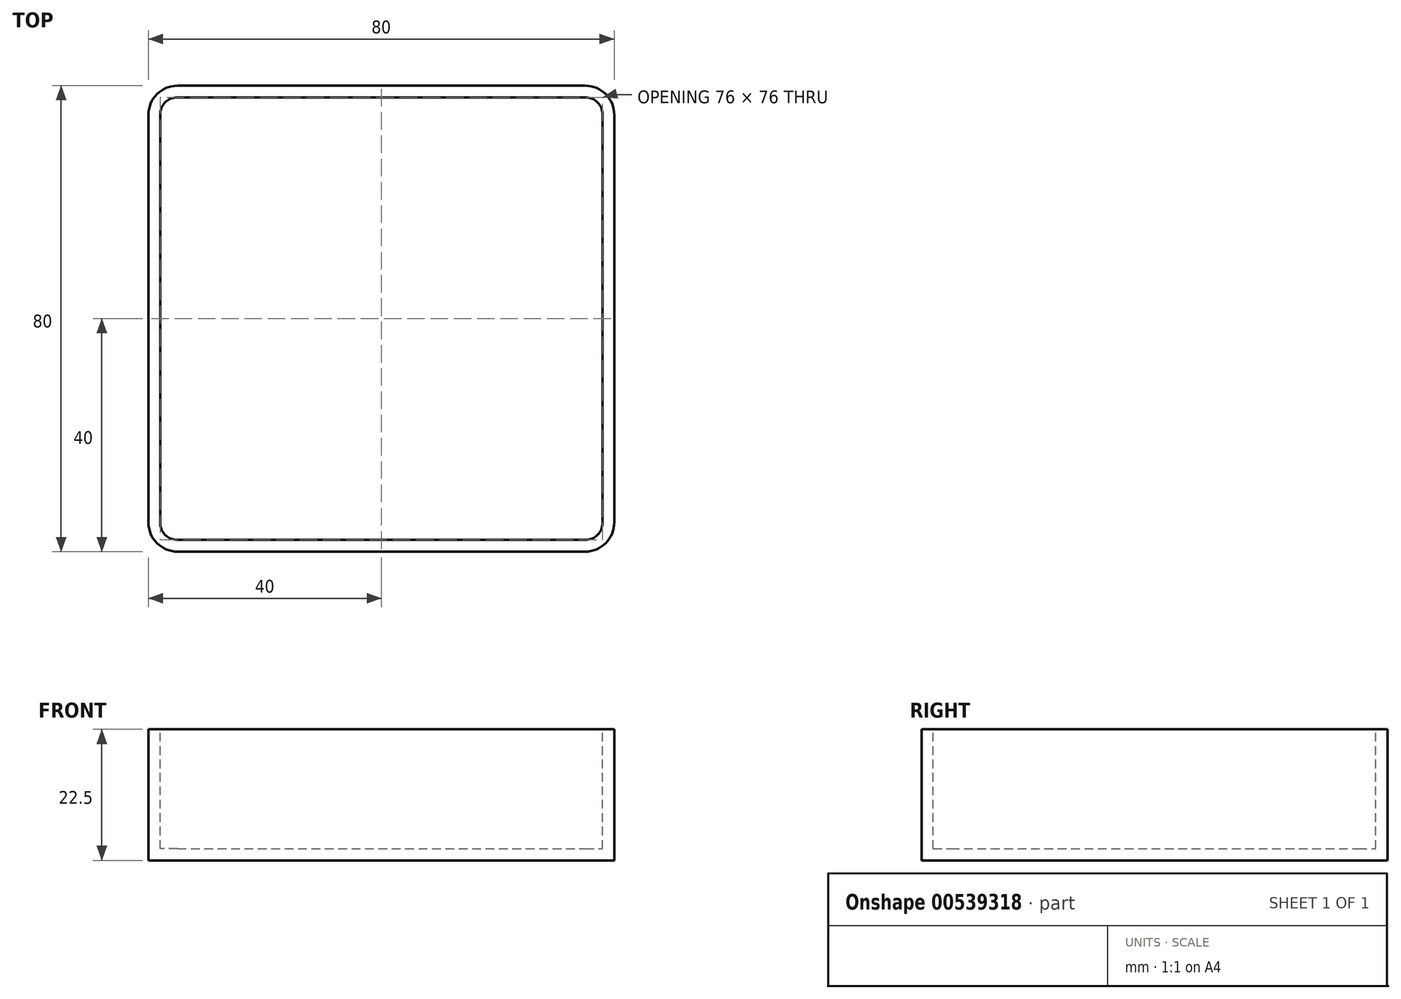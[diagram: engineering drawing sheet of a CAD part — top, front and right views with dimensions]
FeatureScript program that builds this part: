
annotation { "Feature Type Name" : "Feature", "Feature Type Description" : "" }
export const myFeature = defineFeature(function(context is Context, id is Id, definition is map)
    precondition{}
    {
        {
            var Q0;
            Q0=qCreatedBy(makeId("Top.planeOp"),FACE);
            var sketch = newSketch(context, id + "F0", { "sketchPlane" : qUnion([Q0])});
            skLineSegment(sketch, "E0.bottom", {"start": v(0, 0) * mm, "end": v(80, 0) * mm});
            skLineSegment(sketch, "E0.top", {"start": v(0, 80) * mm, "end": v(80, 80) * mm});
            skLineSegment(sketch, "E0.left", {"start": v(0, 0) * mm, "end": v(0, 80) * mm});
            skLineSegment(sketch, "E0.right", {"start": v(80, 0) * mm, "end": v(80, 80) * mm});
            skSolve(sketch);
        }
        {
            var Q0;
            Q0 = qSketchRegion(id + "F0", true);
            extrude(context, id + "F1", {"entities" : qUnion([Q0]), "depth" : 22.5 * mm, "offsetDistance" : 25 * mm});
        }
        {
            var Q0;
            Q0=makeQuery(id+"F1.opExtrude","SWEPT_EDGE",EDGE,{"disambiguationData":[OSD([sQuery(id+"F0.wireOp",EDGE,"E0.bottom"),sQuery(id+"F0.wireOp",EDGE,"E0.right")])]});
            var Q1;
            Q1=makeQuery(id+"F1.opExtrude","SWEPT_EDGE",EDGE,{"disambiguationData":[OSD([sQuery(id+"F0.wireOp",EDGE,"E0.top"),sQuery(id+"F0.wireOp",EDGE,"E0.right")])]});
            var Q2;
            Q2=makeQuery(id+"F1.opExtrude","SWEPT_EDGE",EDGE,{"disambiguationData":[OSD([sQuery(id+"F0.wireOp",EDGE,"E0.top"),sQuery(id+"F0.wireOp",EDGE,"E0.left")])]});
            var Q3;
            Q3=makeQuery(id+"F1.opExtrude","SWEPT_EDGE",EDGE,{"disambiguationData":[OSD([sQuery(id+"F0.wireOp",EDGE,"E0.bottom"),sQuery(id+"F0.wireOp",EDGE,"E0.left")])]});
            fillet(context, id + "F2", {"entities" : qUnion([Q0, Q1, Q2, Q3]), "radius" : 5 * mm, "tangentPropagation" : true, "allowEdgeOverflow" : false});
        }
        {
            var Q0;
            Q0=makeQuery(id+"F1.opExtrude","CAP_FACE",FACE,{"disambiguationData":[OSD([sQuery(id+"F0.wireOp",EDGE,"E0.bottom"),sQuery(id+"F0.wireOp",EDGE,"E0.top"),sQuery(id+"F0.wireOp",EDGE,"E0.left"),sQuery(id+"F0.wireOp",EDGE,"E0.right")])],"isStart":false});
            shell(context, id + "F3", {"entities" : qUnion([Q0]), "thickness" : 2 * mm});
        }
    });
